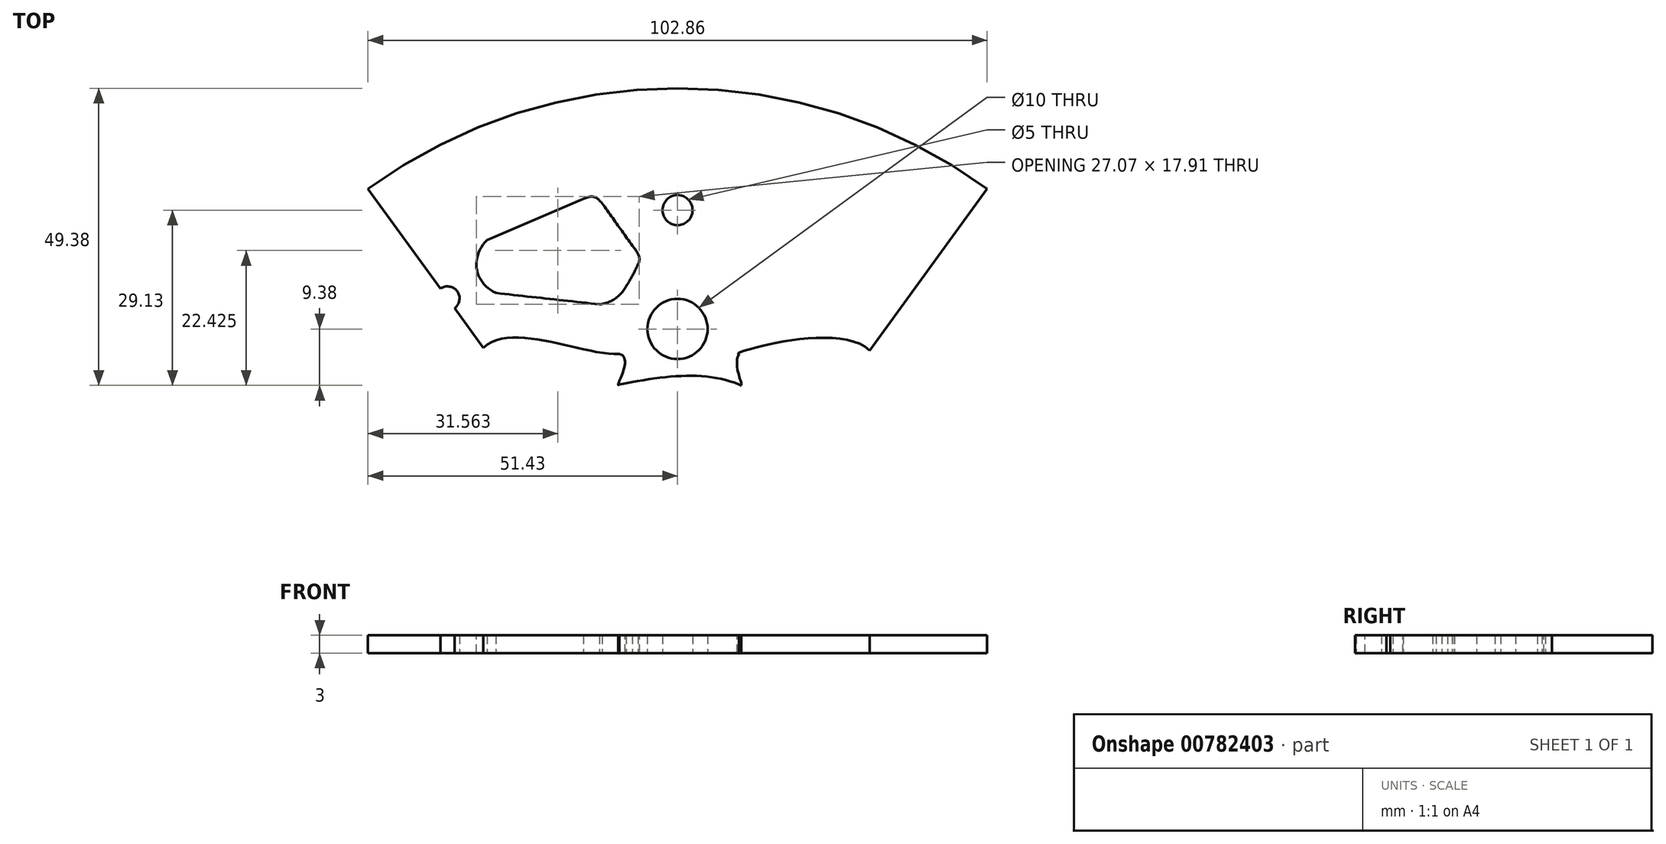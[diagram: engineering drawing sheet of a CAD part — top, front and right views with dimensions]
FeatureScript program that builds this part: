
annotation { "Feature Type Name" : "Feature", "Feature Type Description" : "" }
export const myFeature = defineFeature(function(context is Context, id is Id, definition is map)
    precondition{}
    {
        {
            var Q0;
            Q0=qCreatedBy(makeId("Top.planeOp"),FACE);
            var sketch = newSketch(context, id + "F0", { "sketchPlane" : qUnion([Q0])});
            skArc(sketch, "E0", {"start": v(51.43, 70.79) * mm, "mid": v(0, 87.5) * mm, "end": v(-51.43, 70.79) * mm});
            skLineSegment(sketch, "E1", {"start": v(0, 116.87) * mm, "end": v(0, -107.63) * mm, "construction": true});
            skLineSegment(sketch, "E2", {"start": v(-130.83, 0) * mm, "end": v(132.05, 0) * mm, "construction": true});
            skLineSegment(sketch, "E3", {"start": v(51.43, 70.79) * mm, "end": v(0, 0) * mm});
            skLineSegment(sketch, "E4.MirrorCS", {"start": v(-51.43, 70.79) * mm, "end": v(0, 0) * mm});
            skSolve(sketch);
        }
        {
            var Q0;
            Q0 = qSketchRegion(id + "F0", true);
            extrude(context, id + "F1", {"entities" : qUnion([Q0]), "depth" : 3 * mm, "offsetDistance" : 25 * mm});
        }
        {
            var Q0;
            Q0=qCreatedBy(makeId("Top.planeOp"),FACE);
            var sketch = newSketch(context, id + "F2", { "sketchPlane" : qUnion([Q0])});
            skCircle(sketch, "E5", {"center": v(-38.22, 52.58) * mm, "radius": 2 * mm});
            skSolve(sketch);
        }
        {
            var Q0;
            Q0=makeQuery(id+"F2.imprint","IMPRINT",FACE,{"disambiguationData":[TD([[makeQuery(id+"F2.imprint","IMPRINT",EDGE,{"derivedFrom":sQuery(id+"F2.wireOp",EDGE,"E5")}),1.0]])]});
            var Q1;
            Q1=sQuery(id+"F2.wireOp",EDGE,"E5");
            extrude(context, id + "F3", {"entities" : qUnion([Q0]), "operationType" : NewBodyOperationType.REMOVE, "surfaceEntities" : qUnion([Q1]), "depth" : 13.4 * mm, "offsetDistance" : 25 * mm});
        }
        {
            var Q0;
            Q0=qCreatedBy(makeId("Top.planeOp"),FACE);
            var sketch = newSketch(context, id + "F4", { "sketchPlane" : qUnion([Q0])});
            skLineSegment(sketch, "E6", {"start": v(0, 0) * mm, "end": v(0, 47.5) * mm});
            skCircle(sketch, "E7", {"center": v(0, 47.5) * mm, "radius": 5 * mm});
            skSolve(sketch);
        }
        {
            var Q0;
            Q0=makeQuery(id+"F4.imprint","IMPRINT",FACE,{"disambiguationData":[TD([[makeQuery(id+"F4.imprint","IMPRINT",EDGE,{"derivedFrom":sQuery(id+"F4.wireOp",EDGE,"E7")}),1.0]])]});
            extrude(context, id + "F5", {"entities" : qUnion([Q0]), "operationType" : NewBodyOperationType.REMOVE, "depth" : 15.1 * mm, "offsetDistance" : 25 * mm});
        }
        {
            var Q0;
            Q0=qCreatedBy(makeId("Top.planeOp"),FACE);
            var sketch = newSketch(context, id + "F6", { "sketchPlane" : qUnion([Q0])});
            skFitSpline(sketch, "E8", {"points": [v(-32.37, 44.26) * mm, v(-9.65, 43.34) * mm], "startDerivative": vector(13.95, 13.95) * mm, "endDerivative": vector(19.88, 0.48) * mm});
            skFitSpline(sketch, "E9", {"points": [v(-9.65, 43.34) * mm, v(-9.65, 38.27) * mm], "startDerivative": vector(7.66, -1.92) * mm, "endDerivative": vector(3.41, 2.55) * mm});
            skFitSpline(sketch, "E10", {"points": [v(-9.65, 38.27) * mm, v(10.23, 38.27) * mm], "startDerivative": vector(23.08, 4.56) * mm, "endDerivative": vector(16.88, -7) * mm});
            skFitSpline(sketch, "E11", {"points": [v(10.23, 38.27) * mm, v(10.23, 43.34) * mm], "startDerivative": vector(3.9, -2.82) * mm, "endDerivative": vector(3.85, 6.25) * mm});
            skFitSpline(sketch, "E12", {"points": [v(10.23, 43.34) * mm, v(32.46, 43.34) * mm], "startDerivative": vector(-6.82, 0) * mm, "endDerivative": vector(12.99, -18.25) * mm});
            skLineSegment(sketch, "E13", {"start": v(-32.37, 44.26) * mm, "end": v(0, 0) * mm});
            skLineSegment(sketch, "E14", {"start": v(32.46, 43.34) * mm, "end": v(0, 0) * mm});
            skSolve(sketch);
        }
        {
            var Q0;
            Q0 = qSketchRegion(id + "F6", true);
            extrude(context, id + "F7", {"entities" : qUnion([Q0]), "operationType" : NewBodyOperationType.REMOVE, "depth" : 28 * mm, "offsetDistance" : 25 * mm});
        }
        {
            var Q0;
            Q0=qCreatedBy(makeId("Top.planeOp"),FACE);
            var sketch = newSketch(context, id + "F8", { "sketchPlane" : qUnion([Q0])});
            skFitSpline(sketch, "E15", {"points": [v(-30.19, 53.48) * mm, v(-12.98, 51.59) * mm], "startDerivative": vector(17.15, -1.94) * mm, "endDerivative": vector(17.15, -1.94) * mm});
            skFitSpline(sketch, "E16", {"points": [v(-12.98, 51.59) * mm, v(-8.54, 54.6) * mm], "startDerivative": vector(5.6, 0.42) * mm, "endDerivative": vector(2.21, 4.6) * mm});
            skFitSpline(sketch, "E17", {"points": [v(-31.65, 62.29) * mm, v(-30.19, 53.48) * mm], "startDerivative": vector(-8.54, -8.94) * mm, "endDerivative": vector(10.98, -5.38) * mm});
            skFitSpline(sketch, "E18", {"points": [v(-31.65, 62.29) * mm, v(-15.63, 69.12) * mm], "startDerivative": vector(16.02, 6.84) * mm, "endDerivative": vector(16.02, 6.84) * mm});
            skFitSpline(sketch, "E19", {"points": [v(-15.63, 69.12) * mm, v(-12.53, 68.4) * mm], "startDerivative": vector(4.75, 1.92) * mm, "endDerivative": vector(3.38, -3.73) * mm});
            skFitSpline(sketch, "E20", {"points": [v(-12.53, 68.4) * mm, v(-7.48, 61.32) * mm], "startDerivative": vector(5.1, -7.07) * mm, "endDerivative": vector(5.1, -7.07) * mm});
            skFitSpline(sketch, "E21", {"points": [v(-7.48, 61.32) * mm, v(-6.53, 58.3) * mm], "startDerivative": vector(3.04, -3.61) * mm, "endDerivative": vector(-1.44, -2.79) * mm});
            skFitSpline(sketch, "E22", {"points": [v(-6.53, 58.3) * mm, v(-8.54, 54.6) * mm], "startDerivative": vector(-2.02, -4.35) * mm, "endDerivative": vector(-2.47, -3.77) * mm});
            skSolve(sketch);
        }
        {
            var Q0;
            Q0 = qSketchRegion(id + "F8", true);
            extrude(context, id + "F9", {"entities" : qUnion([Q0]), "operationType" : NewBodyOperationType.REMOVE, "depth" : 40.9 * mm, "offsetDistance" : 25 * mm});
        }
        {
            var Q0;
            Q0=qCreatedBy(makeId("Top.planeOp"),FACE);
            var sketch = newSketch(context, id + "F10", { "sketchPlane" : qUnion([Q0])});
            skCircle(sketch, "E23", {"center": v(0, 67.25) * mm, "radius": 2.5 * mm});
            skSolve(sketch);
        }
        {
            var Q0;
            Q0 = qSketchRegion(id + "F10", true);
            extrude(context, id + "F11", {"entities" : qUnion([Q0]), "operationType" : NewBodyOperationType.REMOVE, "depth" : 30.3 * mm, "offsetDistance" : 25 * mm});
        }
        {
            var Q0;
            Q0 = qSketchRegion(id + "F8", true);
            extrude(context, id + "F12", {"entities" : qUnion([Q0]), "operationType" : NewBodyOperationType.REMOVE, "depth" : 32.7 * mm, "offsetDistance" : 25 * mm});
        }
    });
